# Revit family: Faucet-Bath_Handle_Trim-KOHLER-Refinia-K-T5325
name_source: partatom
category: Plumbing Fixtures
revit_build: Autodesk Revit 2015 (Build: 20140606_1530(x64)
units: mm (PartAtom-declared; Revit-internal decimal feet)

## types (2) — shared parameters
ADA Compliant = Yes
Assembly Code = D2010
CW Connection = Yes
Cold Water Inlet = Cold Water Inlet
Date Modified = 04/29/2019
Default Elevation = 36"
Description = Lever handles valve trim, valve not included
Drain Included = No
Flow Rate = 0 GPM
HW Connection = Yes
Handle Clearance = 3 1/2"
Height = 4 7/8"
Hot Water Inlet = Hot Water Inlet
Length = 2 3/4"
Manufacturer = KOHLER Co.
MasterFormat 1995 = 15410
MasterFormat 2004 = 22.41.39
Material = Metal construction
Pressure = 0.00 psi
Product Documentation Link = https://www.us.kohler.com
Product Name = Refinia
Product Page URL = http://www.us.kohler.com
Spout Reach = 0"
URL = https://www.us.kohler.com
Vent Connection = No
Waste Connection = No
Waste Water Outlet = Waste Water Outlet
WaterSense Certified = No

## per-type parameters (varying)
| type | Finish | Model | Type |
| CP-Polished Chrome | Kohler-Metal-CP-Polished_Chrome | K-T5325-4-CP | 1 |
| BN-Vibrant Brushed Nickel | Kohler-Metal-BN-Vibrant_Brushed_Nickel | K-T5325-4-BN | 2 |

## geometry (parser evidence)
native form markers: Sweep x6
no freeform markers — native parametric forms only
